# Revit family: Serena 7030
name_source: partatom
category: Furniture
revit_build: Autodesk Revit MEP 2012 (Build: 20110309_2315(x64)
units: mm (PartAtom-declared; Revit-internal decimal feet)

## types (1)
- Serena 7030
    BIM object Category = Furniture
    Depth (mm) = 20 mm  [stored 0.0656168 ft]
    Design country = Sweden
    Edition number = 1
    Height (mm) = 800 mm  [stored 2.62467 ft]
    IFC Classification = Furniture
    Manufacture country = Sweden
    Manufacturer = Stolab
    Material = Birch_horr
    Model = Serena 7030
    Product SKU = 7030
    Product family = Storage Units Hallway
    Product group = Serena
    URL = http://stolab.bimobject.com
    Weight Net (kg) = 0 mm  [stored 0 ft]
    Width (mm) = 400 mm  [stored 1.31234 ft]

note: [stored X ft] marks values corroborated as IEEE doubles in the binary element streams (Revit-internal decimal feet)

## geometry (parser evidence)
native form markers: Blend x14, Sweep x1
no freeform markers — native parametric forms only
